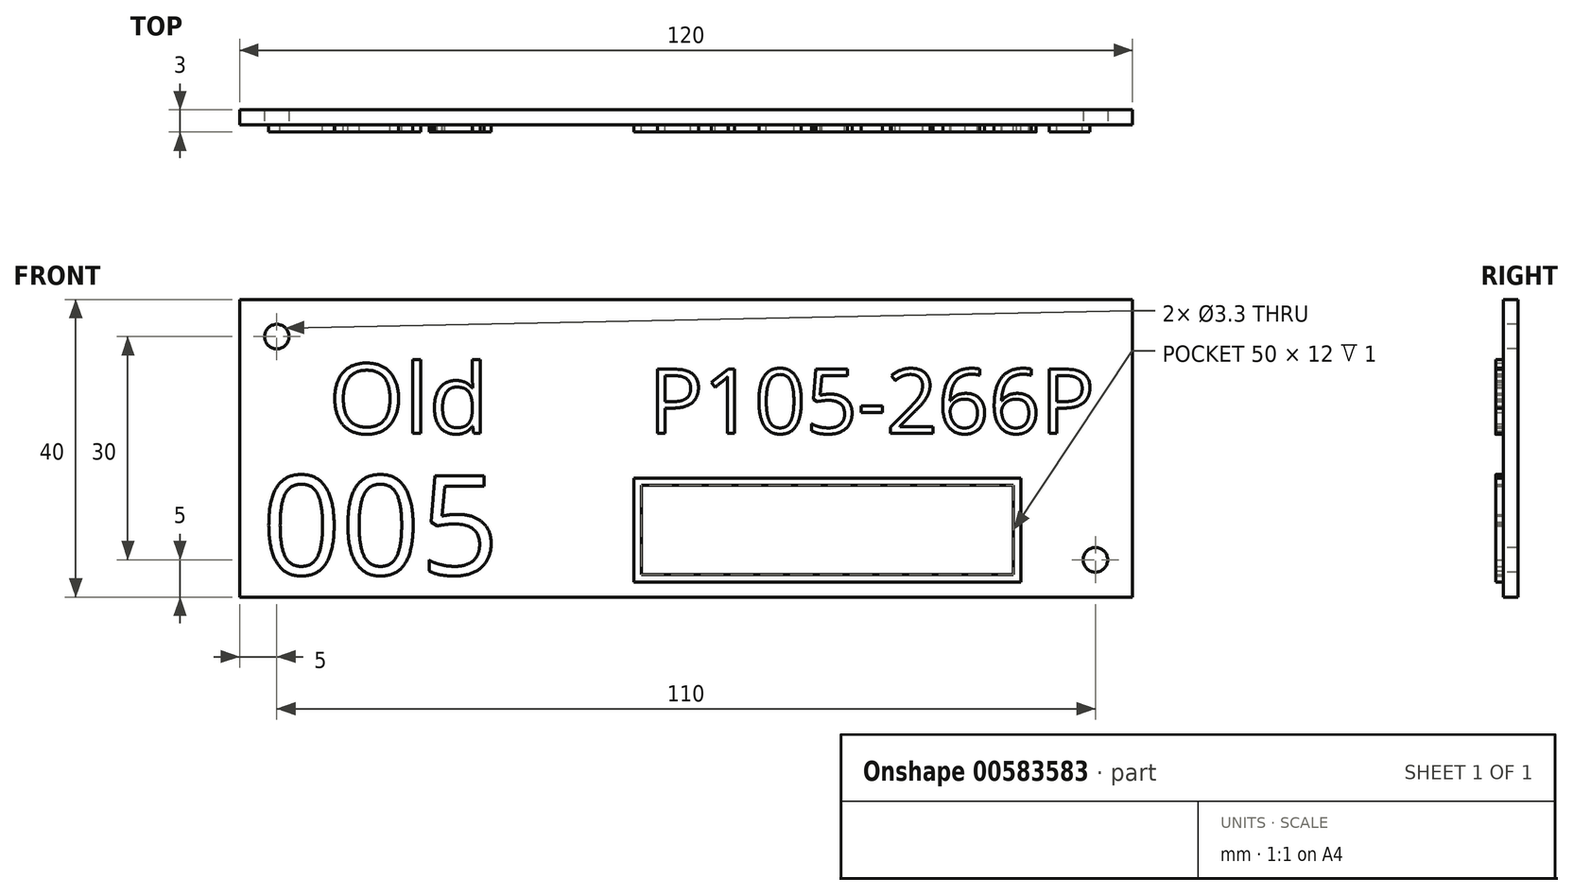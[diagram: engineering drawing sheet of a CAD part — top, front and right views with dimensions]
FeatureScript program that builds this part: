
annotation { "Feature Type Name" : "Feature", "Feature Type Description" : "" }
export const myFeature = defineFeature(function(context is Context, id is Id, definition is map)
    precondition{}
    {
        {
            var Q0;
            Q0=qCreatedBy(makeId("Front.planeOp"),FACE);
            var sketch = newSketch(context, id + "F0", { "sketchPlane" : qUnion([Q0])});
            skLineSegment(sketch, "E0.bottom", {"start": v(60, -20) * mm, "end": v(-60, -20) * mm});
            skLineSegment(sketch, "E0.top", {"start": v(60, 20) * mm, "end": v(-60, 20) * mm});
            skLineSegment(sketch, "E0.left", {"start": v(60, -20) * mm, "end": v(60, 20) * mm});
            skLineSegment(sketch, "E0.right", {"start": v(-60, -20) * mm, "end": v(-60, 20) * mm});
            skPoint(sketch, "E0.middle", {"position": v(0, 0) * mm});
            skSolve(sketch);
        }
        {
            var Q0;
            Q0=makeQuery(id+"F0.imprint","IMPRINT",FACE,{"disambiguationData":[TD([[makeQuery(id+"F0.imprint","IMPRINT",EDGE,{"derivedFrom":sQuery(id+"F0.wireOp",EDGE,"E0.bottom")}),-1.0]])]});
            extrude(context, id + "F1", {"entities" : qUnion([Q0]), "depth" : 2 * mm});
        }
        {
            var Q0;
            Q0=makeQuery(id+"F1.opExtrude","CAP_FACE",FACE,{"disambiguationData":[OSD([sQuery(id+"F0.wireOp",EDGE,"E0.bottom"),sQuery(id+"F0.wireOp",EDGE,"E0.top"),sQuery(id+"F0.wireOp",EDGE,"E0.left"),sQuery(id+"F0.wireOp",EDGE,"E0.right")])],"isStart":false});
            var sketch = newSketch(context, id + "F2", { "sketchPlane" : qUnion([Q0])});
            skPoint(sketch, "E1", {"position": v(-55, 15) * mm});
            skPoint(sketch, "E2", {"position": v(55, -15) * mm});
            skSolve(sketch);
        }
        {
            var Q0;
            Q0=sQuery(id+"F2.wireOp",VERTEX,"E1");
            var Q1;
            Q1=sQuery(id+"F2.wireOp",VERTEX,"E2");
            var Q2;
            Q2=makeQuery(id+"F1.opExtrude","SWEPT_BODY",BODY,{"disambiguationData":[OSD([sQuery(id+"F0.wireOp",EDGE,"E0.bottom"),sQuery(id+"F0.wireOp",EDGE,"E0.top"),sQuery(id+"F0.wireOp",EDGE,"E0.left"),sQuery(id+"F0.wireOp",EDGE,"E0.right")])]});
            hole(context, id + "F3", {"style" : HoleStyle.SIMPLE, "endStyle" : HoleEndStyle.THROUGH, "holeDiameter" : 3.3 * mm, "locations" : qUnion([Q0, Q1]), "scope" : qUnion([Q2]), "isTappedThrough" : true});
        }
        {
            var Q0;
            Q0=makeQuery(id+"F1.opExtrude","CAP_FACE",FACE,{"disambiguationData":[OSD([sQuery(id+"F0.wireOp",EDGE,"E0.bottom"),sQuery(id+"F0.wireOp",EDGE,"E0.top"),sQuery(id+"F0.wireOp",EDGE,"E0.left"),sQuery(id+"F0.wireOp",EDGE,"E0.right")])],"isStart":false});
            var sketch = newSketch(context, id + "F4", { "sketchPlane" : qUnion([Q0])});
            skText(sketch, "E3", { "text": "P105-266P", "fontName": "OpenSans-Regular.ttf"});
            const initialGuessF4  = {"E3": [-0.005, 0.002, 1, 0, 0.0087]};
            skSetInitialGuess(sketch, initialGuessF4);
            skSolve(sketch);
        }
        {
            var Q0;
            Q0=qSketchRegion(id+"F4",true);
            extrude(context, id + "F5", {"entities" : qUnion([Q0]), "operationType" : NewBodyOperationType.ADD, "depth" : 1 * mm, "offsetDistance" : 25 * mm});
        }
        {
            var Q0;
            {var subQ0=sQuery(id+"F0.wireOp",EDGE,"E0.top");var subQ1=sQuery(id+"F0.wireOp",EDGE,"E0.left");var subQ2=sQuery(id+"F0.wireOp",EDGE,"E0.right");var subQ3=sQuery(id+"F0.wireOp",EDGE,"E0.bottom");Q0=makeQuery(id+"F5.boolean.opBoolean","SPLIT",FACE,{"disambiguationData":[TD([makeQuery(id+"F1.opExtrude","SWEPT_FACE",FACE,{"disambiguationData":[OSD([subQ3])]})])],"derivedFrom":makeQuery(id+"F1.opExtrude","CAP_FACE",FACE,{"disambiguationData":[OSD([subQ3,subQ0,subQ1,subQ2])],"isStart":false})});}
            var sketch = newSketch(context, id + "F6", { "sketchPlane" : qUnion([Q0])});
            skText(sketch, "E4", { "text": "005", "fontName": "OpenSans-Regular.ttf"});
            const initialGuessF6  = {"E4": [-0.057, -0.017, 1, 0, 0.01338]};
            skSetInitialGuess(sketch, initialGuessF6);
            skSolve(sketch);
        }
        {
            var Q0;
            Q0=qSketchRegion(id+"F6",true);
            extrude(context, id + "F7", {"entities" : qUnion([Q0]), "operationType" : NewBodyOperationType.ADD, "depth" : 1 * mm});
        }
        {
            var Q0;
            {var subQ46=sQuery(id+"F0.wireOp",EDGE,"E0.top");var subQ48=sQuery(id+"F0.wireOp",EDGE,"E0.left");var subQ66=sQuery(id+"F0.wireOp",EDGE,"E0.right");var subQ76=sQuery(id+"F0.wireOp",EDGE,"E0.bottom");var subQ77=makeQuery(id+"F1.opExtrude","SWEPT_FACE",FACE,{"disambiguationData":[OSD([subQ76])]});Q0=makeQuery(id+"F7.boolean.opBoolean","SPLIT",FACE,{"disambiguationData":[TD([subQ77])],"derivedFrom":makeQuery(id+"F5.boolean.opBoolean","SPLIT",FACE,{"disambiguationData":[TD([subQ77])],"derivedFrom":makeQuery(id+"F1.opExtrude","CAP_FACE",FACE,{"disambiguationData":[OSD([subQ76,subQ46,subQ48,subQ66])],"isStart":false})})});}
            var sketch = newSketch(context, id + "F8", { "sketchPlane" : qUnion([Q0])});
            skLineSegment(sketch, "E5.bottom", {"start": v(45, -18) * mm, "end": v(-7, -18) * mm});
            skLineSegment(sketch, "E5.top", {"start": v(45, -4) * mm, "end": v(-7, -4) * mm});
            skLineSegment(sketch, "E5.left", {"start": v(45, -18) * mm, "end": v(45, -4) * mm});
            skLineSegment(sketch, "E5.right", {"start": v(-7, -18) * mm, "end": v(-7, -4) * mm});
            skPoint(sketch, "E5.middle", {"position": v(19, -11) * mm});
            skLineSegment(sketch, "E6.0", {"start": v(44, -5) * mm, "end": v(-6, -5) * mm});
            skLineSegment(sketch, "E6.1", {"start": v(44, -17) * mm, "end": v(44, -5) * mm});
            skLineSegment(sketch, "E6.2", {"start": v(44, -17) * mm, "end": v(-6, -17) * mm});
            skLineSegment(sketch, "E6.3", {"start": v(-6, -17) * mm, "end": v(-6, -5) * mm});
            skSolve(sketch);
        }
        {
            var Q0;
            Q0=makeQuery(id+"F8.imprint","IMPRINT",FACE,{"disambiguationData":[TD([[makeQuery(id+"F8.imprint","IMPRINT",EDGE,{"derivedFrom":sQuery(id+"F8.wireOp",EDGE,"E5.bottom")}),-1.0]])]});
            extrude(context, id + "F9", {"entities" : qUnion([Q0]), "operationType" : NewBodyOperationType.ADD, "depth" : 1 * mm});
        }
        {
            var Q0;
            {var subQ53=sQuery(id+"F0.wireOp",EDGE,"E0.top");var subQ58=sQuery(id+"F0.wireOp",EDGE,"E0.bottom");var subQ59=makeQuery(id+"F1.opExtrude","SWEPT_FACE",FACE,{"disambiguationData":[OSD([subQ58])]});var subQ75=sQuery(id+"F0.wireOp",EDGE,"E0.left");var subQ83=sQuery(id+"F0.wireOp",EDGE,"E0.right");Q0=makeQuery(id+"F9.boolean.opBoolean","SPLIT",FACE,{"disambiguationData":[TD([subQ59])],"derivedFrom":makeQuery(id+"F7.boolean.opBoolean","SPLIT",FACE,{"disambiguationData":[TD([subQ59])],"derivedFrom":makeQuery(id+"F5.boolean.opBoolean","SPLIT",FACE,{"disambiguationData":[TD([subQ59])],"derivedFrom":makeQuery(id+"F1.opExtrude","CAP_FACE",FACE,{"disambiguationData":[OSD([subQ58,subQ53,subQ75,subQ83])],"isStart":false})})})});}
            var sketch = newSketch(context, id + "F10", { "sketchPlane" : qUnion([Q0])});
            skText(sketch, "E7", { "text": "Old", "fontName": "OpenSans-Regular.ttf"});
            const initialGuessF10  = {"E7": [-0.048, 0.002, 1, 0, 0.00939]};
            skSetInitialGuess(sketch, initialGuessF10);
            skSolve(sketch);
        }
        {
            var Q0;
            Q0 = qSketchRegion(id + "F10", true);
            extrude(context, id + "F11", {"entities" : qUnion([Q0]), "operationType" : NewBodyOperationType.ADD, "depth" : 1 * mm, "offsetDistance" : 25 * mm});
        }
    });
